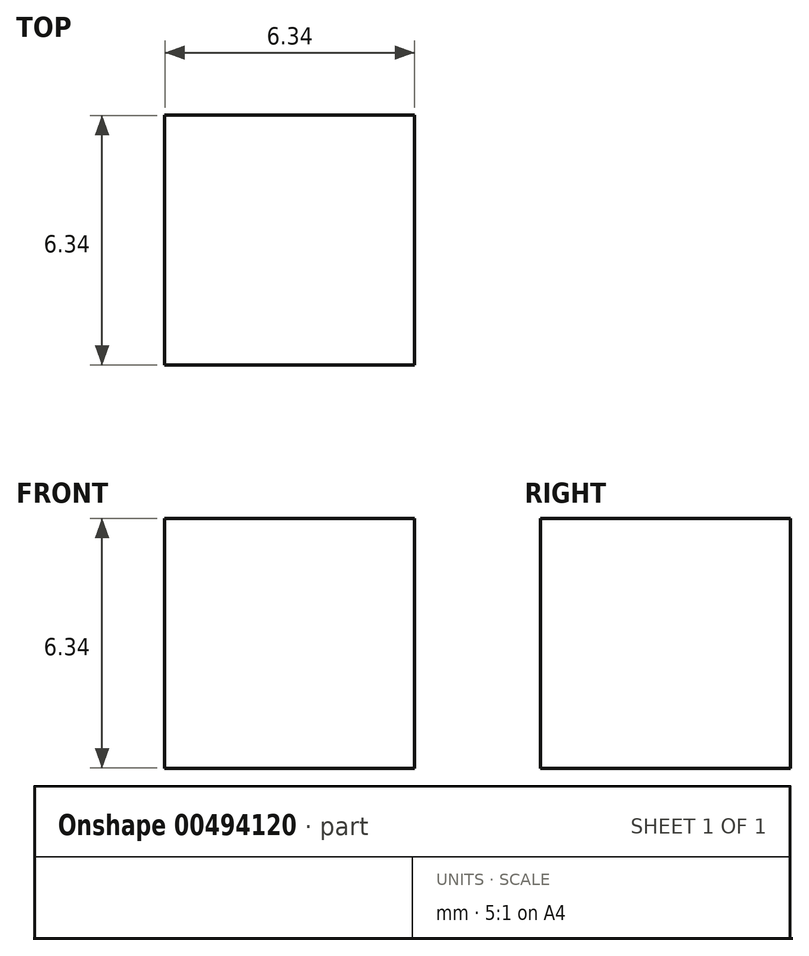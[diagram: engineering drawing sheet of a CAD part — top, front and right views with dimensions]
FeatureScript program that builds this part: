
annotation { "Feature Type Name" : "Feature", "Feature Type Description" : "" }
export const myFeature = defineFeature(function(context is Context, id is Id, definition is map)
    precondition{}
    {
        {
            var Q0;
            Q0=qCreatedBy(makeId("Right.planeOp"),FACE);
            var sketch = newSketch(context, id + "F0", { "sketchPlane" : qUnion([Q0])});
            skLineSegment(sketch, "E0.bottom", {"start": v(-3.17, 3.17) * mm, "end": v(3.18, 3.17) * mm});
            skLineSegment(sketch, "E0.top", {"start": v(-3.17, -3.18) * mm, "end": v(3.18, -3.18) * mm});
            skLineSegment(sketch, "E0.left", {"start": v(-3.17, 3.18) * mm, "end": v(-3.17, -3.18) * mm});
            skLineSegment(sketch, "E0.right", {"start": v(3.18, 3.17) * mm, "end": v(3.18, -3.18) * mm});
            skPoint(sketch, "E0.middle", {"position": v(0, 0) * mm});
            skSolve(sketch);
        }
        {
            var Q0;
            Q0=makeQuery(id+"F0.imprint","IMPRINT",FACE,{"disambiguationData":[TD([[makeQuery(id+"F0.imprint","IMPRINT",EDGE,{"derivedFrom":sQuery(id+"F0.wireOp",EDGE,"E0.bottom")}),-1.0]])]});
            extrude(context, id + "F1", {"entities" : qUnion([Q0]), "endBound" : BoundingType.SYMMETRIC, "depth" : 6.35 * mm});
        }
    });
